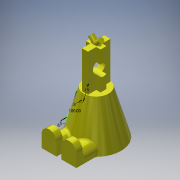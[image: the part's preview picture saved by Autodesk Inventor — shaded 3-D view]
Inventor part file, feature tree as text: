
AUTODESK INVENTOR PART (.ipt)
format: ipt  version: 2019 (Build 230136000, 136)  size: 402,432 bytes
history: native  units: mm
features: sketch x9, other x6, extrude x6, mirror x3, revolve x2, fillet x2, projected_geometry x2, pattern_linear x1, reference x1
ambient origin geometry x8: Origin, YZ Plane, XZ Plane, XY Plane, X Axis, Y Axis, Z Axis, Center Point
bodies: Body1 (feature_tree)
feature tree (32):
  other  "ソリッド1"
  revolve  "回転1"
  extrude  "脚"  TaperAngle=90.0deg  [1 undecoded]
  extrude  "足"  Depth=35.0mm
  sketch  "スケッチ7"
  other  "作業平面3"
  sketch  "スケッチ14"
  mirror  "ミラー1"
  sketch  "スケッチ9"
  other  "作業平面4"
  extrude  "押し出し4"  Depth=20.0mm
  extrude  "押し出し5"  Depth=10.0mm
  revolve  "回転2"
  mirror  "ミラー3"
  fillet  "フィレット1"  Radius=25.0mm
  fillet  "フィレット2"  Radius=5.0mm
  extrude  "押し出し6"  Depth=4.8mm
  pattern_linear  "矩形状パターン2"  Spacing1=18.0mm  [1 undecoded]
  sketch  "スケッチ13"
  extrude  "押し出し7"  Depth=11.8mm
  mirror  "ミラー4"
  sketch  "スケッチ1"
  sketch  "スケッチ6"
  sketch  "スケッチ10"
  reference  "参照1"
  sketch  "スケッチ11"
  sketch  "スケッチ12"
  projected_geometry  "投影ループ4"
  projected_geometry  "投影ループ5"
  other  "<userpath>\OneDrive\デスクトップ\mini_robot\mini_robot.iam"
  other  "mini_robot.iam"
  other  "head:1"
note: 2 required parameter values undecoded (feature->parameter linkage not recoverable at this tier; creation-order binding heuristic only, values carry confidence <= 0.55)
